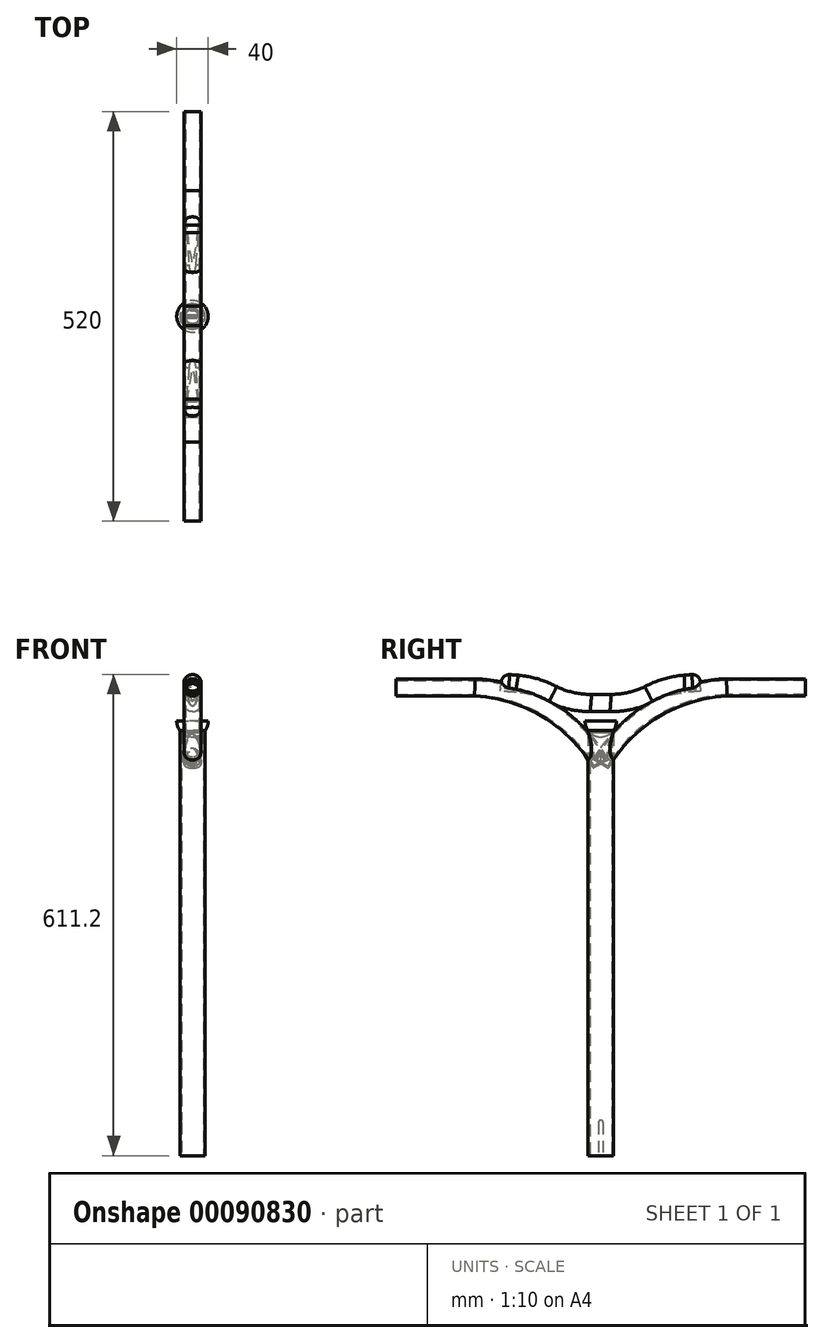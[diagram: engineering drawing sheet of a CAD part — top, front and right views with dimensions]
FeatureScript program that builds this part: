
annotation { "Feature Type Name" : "Feature", "Feature Type Description" : "" }
export const myFeature = defineFeature(function(context is Context, id is Id, definition is map)
    precondition{}
    {
        {
            var Q0;
            Q0=qCreatedBy(makeId("Top.planeOp"),FACE);
            var sketch = newSketch(context, id + "F0", { "sketchPlane" : qUnion([Q0])});
            skCircle(sketch, "E0", {"center": v(0, 0) * mm, "radius": 16 * mm});
            skSolve(sketch);
        }
        {
            var Q0;
            Q0 = qSketchRegion(id + "F0", true);
            extrude(context, id + "F1", {"entities" : qUnion([Q0]), "depth" : 550 * mm});
        }
        {
            var Q0;
            Q0=makeQuery(id+"F1.opExtrude","CAP_FACE",FACE,{"disambiguationData":[OSD([sQuery(id+"F0.wireOp",EDGE,"E0")])],"isStart":false});
            var Q1;
            Q1=makeQuery(id+"F1.opExtrude","SWEPT_BODY",BODY,{"disambiguationData":[OSD([sQuery(id+"F0.wireOp",EDGE,"E0")])]});
            shell(context, id + "F2", {"entities" : qUnion([Q0]), "parts" : qUnion([Q1]), "thickness" : 2 * mm});
        }
        {
            var Q0;
            {var subQ0=sQuery(id+"F0.wireOp",EDGE,"E0");Q0=makeQuery(id+"F2.opShell","OFFSET_FACE",FACE,{"disambiguationData":[OSD([subQ0]),TDD([makeQuery(id+"F1.opExtrude","CAP_FACE",FACE,{"disambiguationData":[OSD([subQ0])],"isStart":true})])]});}
            extrude(context, id + "F3", {"entities" : qUnion([Q0]), "operationType" : NewBodyOperationType.REMOVE, "oppositeDirection" : true, "depth" : 25 * mm});
        }
        {
            var Q0;
            Q0=qCreatedBy(makeId("Right.planeOp"),FACE);
            var sketch = newSketch(context, id + "F4", { "sketchPlane" : qUnion([Q0])});
            skLineSegment(sketch, "E1", {"start": v(-3, 0) * mm, "end": v(-3, 42) * mm});
            skLineSegment(sketch, "E2", {"start": v(0, 45) * mm, "end": v(0, 45) * mm});
            skLineSegment(sketch, "E3", {"start": v(3, 42) * mm, "end": v(3, 0) * mm});
            skPoint(sketch, "E4.visualSharp", {"position": v(3, 45) * mm});
            skArc(sketch, "E4.filletArc", {"start": v(3, 42) * mm, "mid": v(2.12, 44.12) * mm, "end": v(0, 45) * mm});
            skPoint(sketch, "E5.visualSharp", {"position": v(-3, 45) * mm});
            skArc(sketch, "E5.filletArc", {"start": v(0, 45) * mm, "mid": v(-2.12, 44.12) * mm, "end": v(-3, 42) * mm});
            skLineSegment(sketch, "E6", {"start": v(-3, 0) * mm, "end": v(3, 0) * mm});
            skSolve(sketch);
        }
        {
            var Q0;
            Q0=makeQuery(id+"F4.imprint","IMPRINT",FACE,{"disambiguationData":[TD([[makeQuery(id+"F4.imprint","IMPRINT",EDGE,{"derivedFrom":sQuery(id+"F4.wireOp",EDGE,"E1")}),-1.0]])]});
            extrude(context, id + "F5", {"entities" : qUnion([Q0]), "operationType" : NewBodyOperationType.REMOVE, "endBound" : BoundingType.THROUGH_ALL, "oppositeDirection" : true, "depth" : 25 * mm});
        }
        {
            var Q0;
            Q0=qCreatedBy(makeId("Right.planeOp"),FACE);
            var sketch = newSketch(context, id + "F6", { "sketchPlane" : qUnion([Q0])});
            skArc(sketch, "E7", {"start": v(160, 594.8) * mm, "mid": v(67.6, 566.75) * mm, "end": v(0, 497.81) * mm});
            skLineSegment(sketch, "E8", {"start": v(160, 594.8) * mm, "end": v(260, 594.8) * mm});
            skSolve(sketch);
        }
        {
            var Q0;
            Q0=qCreatedBy(makeId("Front.planeOp"),FACE);
            var Q1;
            Q1=sQuery(id+"F6.wireOp",VERTEX,"E8.end");
            cPlane(context, id + "F7", {"entities" : qUnion([Q0, Q1]), "cplaneType" : CPlaneType.PLANE_POINT, "offset" : 25 * mm, "width" : 150 * mm, "height" : 150 * mm});
        }
        {
            var Q0;
            Q0=qCreatedBy(id+"F7.planeOp",FACE);
            var sketch = newSketch(context, id + "F8", { "sketchPlane" : qUnion([Q0])});
            skCircle(sketch, "E9", {"center": v(0, 594.8) * mm, "radius": 11 * mm});
            skSolve(sketch);
        }
        {
            var Q0;
            Q0=makeQuery(id+"F8.imprint","IMPRINT",FACE,{"disambiguationData":[TD([[makeQuery(id+"F8.imprint","IMPRINT",EDGE,{"derivedFrom":sQuery(id+"F8.wireOp",EDGE,"E9")}),1.0]])]});
            var Q1;
            Q1=sQuery(id+"F6.wireOp",EDGE,"E8");
            var Q2;
            Q2=sQuery(id+"F6.wireOp",EDGE,"E7");
            sweep(context, id + "F9", {"operationType" : NewBodyOperationType.ADD, "profiles" : qUnion([Q0]), "path" : qUnion([Q1, Q2])});
        }
        {
            var Q0;
            Q0=makeQuery(id+"F9.opSweep","CAP_FACE",FACE,{"disambiguationData":[OSD([sQuery(id+"F6.wireOp",VERTEX,"E8.end"),sQuery(id+"F8.wireOp",EDGE,"E9")])],"isStart":true});
            shell(context, id + "F10", {"entities" : qUnion([Q0]), "thickness" : 2 * mm});
        }
        {
            var Q0;
            Q0=makeQuery(id+"F1.opExtrude","SWEPT_BODY",BODY,{"disambiguationData":[OSD([sQuery(id+"F0.wireOp",EDGE,"E0")])]});
            var Q1;
            Q1=qCreatedBy(makeId("Front.planeOp"),FACE);
            mirror(context, id + "F11", {"entities" : qUnion([Q0]), "mirrorPlane" : qUnion([Q1])});
        }
        {
            var Q0;
            Q0=qCreatedBy(makeId("Right.planeOp"),FACE);
            var sketch = newSketch(context, id + "F12", { "sketchPlane" : qUnion([Q0])});
            skLineSegment(sketch, "E10", {"start": v(-206.91, 575) * mm, "end": v(263.71, 575) * mm, "construction": true});
            skLineSegment(sketch, "E11", {"start": v(0, 0) * mm, "end": v(0, 916.3) * mm, "construction": true});
            skPoint(sketch, "E12", {"position": v(0, 575) * mm});
            skLineSegment(sketch, "E13", {"start": v(0, 575) * mm, "end": v(12.5, 575) * mm});
            skLineSegment(sketch, "E14", {"start": v(0, 575) * mm, "end": v(-12.5, 575) * mm});
            skArc(sketch, "E15", {"start": v(-60.97, 586.03) * mm, "mid": v(-37.36, 577.8) * mm, "end": v(-12.5, 575) * mm});
            skArc(sketch, "E16", {"start": v(-60.97, 586.03) * mm, "mid": v(-83.03, 595.14) * mm, "end": v(-106.5, 599.46) * mm});
            skLineSegment(sketch, "E17", {"start": v(-106.5, 599.46) * mm, "end": v(-126.45, 601) * mm});
            skArc(sketch, "E18.MirrorCS", {"start": v(60.97, 586.03) * mm, "mid": v(37.36, 577.8) * mm, "end": v(12.5, 575) * mm});
            skLineSegment(sketch, "E19.MirrorCS", {"start": v(106.5, 599.46) * mm, "end": v(126.45, 601) * mm});
            skArc(sketch, "E20.MirrorCS", {"start": v(60.97, 586.03) * mm, "mid": v(83.03, 595.14) * mm, "end": v(106.5, 599.46) * mm});
            skSolve(sketch);
        }
        {
            var Q0;
            Q0=sQuery(id+"F12.wireOp",VERTEX,"E19.MirrorCS.end");
            var Q1;
            Q1=qCreatedBy(id+"F7.planeOp",FACE);
            cPlane(context, id + "F13", {"entities" : qUnion([Q0, Q1]), "cplaneType" : CPlaneType.PLANE_POINT, "offset" : 25 * mm, "width" : 150 * mm, "height" : 150 * mm});
        }
        {
            var Q0;
            Q0=qCreatedBy(id+"F13.planeOp",FACE);
            var sketch = newSketch(context, id + "F14", { "sketchPlane" : qUnion([Q0])});
            skCircle(sketch, "E21", {"center": v(0, 601) * mm, "radius": 11 * mm});
            skSolve(sketch);
        }
        {
            var Q0;
            Q0=makeQuery(id+"F14.imprint","IMPRINT",FACE,{"disambiguationData":[TD([[makeQuery(id+"F14.imprint","IMPRINT",EDGE,{"derivedFrom":sQuery(id+"F14.wireOp",EDGE,"E21")}),1.0]])]});
            var Q1;
            Q1=sQuery(id+"F12.wireOp",EDGE,"E20.MirrorCS");
            var Q2;
            Q2=sQuery(id+"F12.wireOp",EDGE,"E18.MirrorCS");
            var Q3;
            Q3=sQuery(id+"F12.wireOp",EDGE,"E19.MirrorCS");
            var Q4;
            Q4=sQuery(id+"F12.wireOp",EDGE,"E13");
            var Q5;
            Q5=sQuery(id+"F12.wireOp",EDGE,"E14");
            var Q6;
            Q6=sQuery(id+"F12.wireOp",EDGE,"E15");
            var Q7;
            Q7=sQuery(id+"F12.wireOp",EDGE,"E16");
            var Q8;
            Q8=sQuery(id+"F12.wireOp",EDGE,"E17");
            sweep(context, id + "F15", {"operationType" : NewBodyOperationType.ADD, "profiles" : qUnion([Q0]), "path" : qUnion([Q1, Q2, Q3, Q4, Q5, Q6, Q7, Q8])});
        }
        {
            var Q0;
            {var subQ0=sQuery(id+"F14.wireOp",EDGE,"E21");var subQ1=sQuery(id+"F12.wireOp",VERTEX,"E19.MirrorCS.end");Q0=makeQuery(id+"F15.boolean.opBoolean","SPLIT",EDGE,{"disambiguationData":[TD([makeQuery(id+"F9.opSweep","SWEPT_FACE",FACE,{"disambiguationData":[OSD([sQuery(id+"F6.wireOp",EDGE,"E7"),sQuery(id+"F8.wireOp",EDGE,"E9")])]})])],"derivedFrom":makeQuery(id+"F15.opSweep","CAP_EDGE",EDGE,{"disambiguationData":[OSD([subQ1,subQ0])],"isStart":true})});}
            var Q1;
            {var subQ0=sQuery(id+"F8.wireOp",EDGE,"E9");var subQ1=sQuery(id+"F14.wireOp",EDGE,"E21");var subQ2=sQuery(id+"F12.wireOp",VERTEX,"E17.end");Q1=makeQuery(id+"F15.boolean.opBoolean","SPLIT",EDGE,{"disambiguationData":[TD([makeQuery(id+"F11.opPattern","COPY",FACE,{"derivedFrom":makeQuery(id+"F9.boolean.opBoolean","SPLIT",FACE,{"disambiguationData":[TD([makeQuery(id+"F1.opExtrude","SWEPT_FACE",FACE,{"disambiguationData":[OSD([sQuery(id+"F0.wireOp",EDGE,"E0")])]})])],"derivedFrom":makeQuery(id+"F9.opSweep","SWEPT_FACE",FACE,{"disambiguationData":[OSD([sQuery(id+"F6.wireOp",EDGE,"E7"),subQ0])]})}),"instanceName":"1"})])],"derivedFrom":makeQuery(id+"F15.opSweep","CAP_EDGE",EDGE,{"disambiguationData":[OSD([subQ2,subQ1])],"isStart":false})});}
            fillet(context, id + "F16", {"entities" : qUnion([Q0, Q1]), "radius" : 10 * mm, "tangentPropagation" : true, "allowEdgeOverflow" : false});
        }
        {
            var Q0;
            Q0=qCreatedBy(makeId("Right.planeOp"),FACE);
            var sketch = newSketch(context, id + "F17", { "sketchPlane" : qUnion([Q0])});
            skArc(sketch, "E22", {"start": v(-20, 552) * mm, "mid": v(-14.14, 537.86) * mm, "end": v(0, 532) * mm});
            skLineSegment(sketch, "E23", {"start": v(0, 552) * mm, "end": v(0, 532) * mm});
            skLineSegment(sketch, "E24", {"start": v(0, 552) * mm, "end": v(-20, 552) * mm});
            skSolve(sketch);
        }
        {
            var Q0;
            Q0=makeQuery(id+"F17.imprint","IMPRINT",FACE,{"disambiguationData":[TD([[makeQuery(id+"F17.imprint","IMPRINT",EDGE,{"derivedFrom":sQuery(id+"F17.wireOp",EDGE,"E22")}),1.0]])]});
            var Q1;
            Q1=makeQuery(id+"F1.opExtrude","CAP_EDGE",EDGE,{"disambiguationData":[OSD([sQuery(id+"F0.wireOp",EDGE,"E0")])],"isStart":false});
            revolve(context, id + "F18", {"operationType" : NewBodyOperationType.ADD, "entities" : qUnion([Q0]), "axis" : qUnion([Q1]), "revolveType" : RevolveType.FULL});
        }
    });
